SOLIDWORKS PART (.sldprt)
format: sldprt  version: not decoded by parser v0  size: 535,552 bytes
history: native  units: mm
features: sketch x20, extrude x19, fillet x5, plane x3, chamfer x2, material x1, cut_extrude x1 + 1 further entry (+8 scaffold rows collapsed)
feature tree (60):
  scaffold x8  (default folders/planes/origin — collapsed)
  material  "Matériau <non spécifié>"
  "Corps de surface"
  plane  "Face"
  plane  "Dessus"
  plane  "Droite"
  sketch  "Esquisse1"  dims[D1=1.525mm]
  extrude  "Base-Extrusion"  Depth=26mm
  sketch  "Esquisse5"
  cut_extrude  "Enlèv. mat.-Extru.6"  Depth=40mm
  sketch  "Esquisse3"  dims[D1=~2.604436mm]
  extrude  "Boss.-Extru.1"  Depth=25mm
  sketch  "Esquisse4"  dims[D1=~0.724062mm]
  extrude  "Enlèv. mat.-Extru.2"  [1 undecoded]
  sketch  "Esquisse6"  dims[D1=~3.721465mm]
  extrude  "Enlèv. mat.-Extru.3"  [1 undecoded]
  sketch  "Esquisse7"  dims[D1=~3.597719mm]
  extrude  "Enlèv. mat.-Extru.4"  Depth=3mm
  sketch  "Esquisse8"
  extrude  "Boss.-Extru.2"  Depth=2mm
  sketch  "Esquisse9"
  extrude  "Enlèv. mat.-Extru.5"  Depth=32mm
  sketch  "Esquisse12"  dims[D1=~1.458238mm]
  extrude  "Boss.-Extru.3"  Depth=26mm
  sketch  "Esquisse13"  dims[D1=~1.690924mm]
  extrude  "Enlèv. mat.-Extru.8"  Depth=32mm
  sketch  "Esquisse14"  dims[D1=1.5mm]
  extrude  "Enlèv. mat.-Extru.9"  [1 undecoded]
  sketch  "Esquisse15"
  extrude  "Enlèv. mat.-Extru.10"  Depth=3mm
  fillet  "Congé1"  Radius=5mm
  fillet  "Congé2"  Radius=4mm
  chamfer  "Chanfrein1"  Distance=0.5mm Angle=45deg
  sketch  "Esquisse16"
  extrude  "Enlèv. mat.-Extru.12"  Depth=30mm
  sketch  "Esquisse17"  dims[D1=~3.308073mm]
  extrude  "Enlèv. mat.-Extru.13"  Depth=11mm
  sketch  "Esquisse18"  dims[D1=5.0mm]
  extrude  "Boss.-Extru.4"  Depth=1.5mm
  sketch  "Esquisse20"
  extrude  "Enlèv. mat.-Extru.14"  Depth=3mm
  sketch  "Esquisse21"
  extrude  "Boss.-Extru.5"  Depth=7mm
  chamfer  "Chanfrein2"  Distance=7mm
  sketch  "Esquisse22"  dims[D1=1.5mm]
  extrude  "Boss.-Extru.6"  Depth=2mm
  fillet  "Congé3"  Radius=2mm
  fillet  "Congé4"  Radius=5mm
  sketch  "Esquisse23"
  extrude  "Boss.-Extru.7"  Depth=0.3mm
  sketch  "Esquisse25"  dims[D1=~0.629546mm]
  extrude  "Boss.-Extru.8"  Depth=2.5mm
  fillet  "Congé5"  Radius=2mm
decode coverage: 36 of 47 modeling features carry decoded parameters; 1 rows unclassified (native names shown)
note: ~ marks probable driven/reference dimensions
note: 3 parameter values undecoded
summary: no parameter record found for 3 features
note: suppression state not decoded; provenance and decode notes live in map.json
